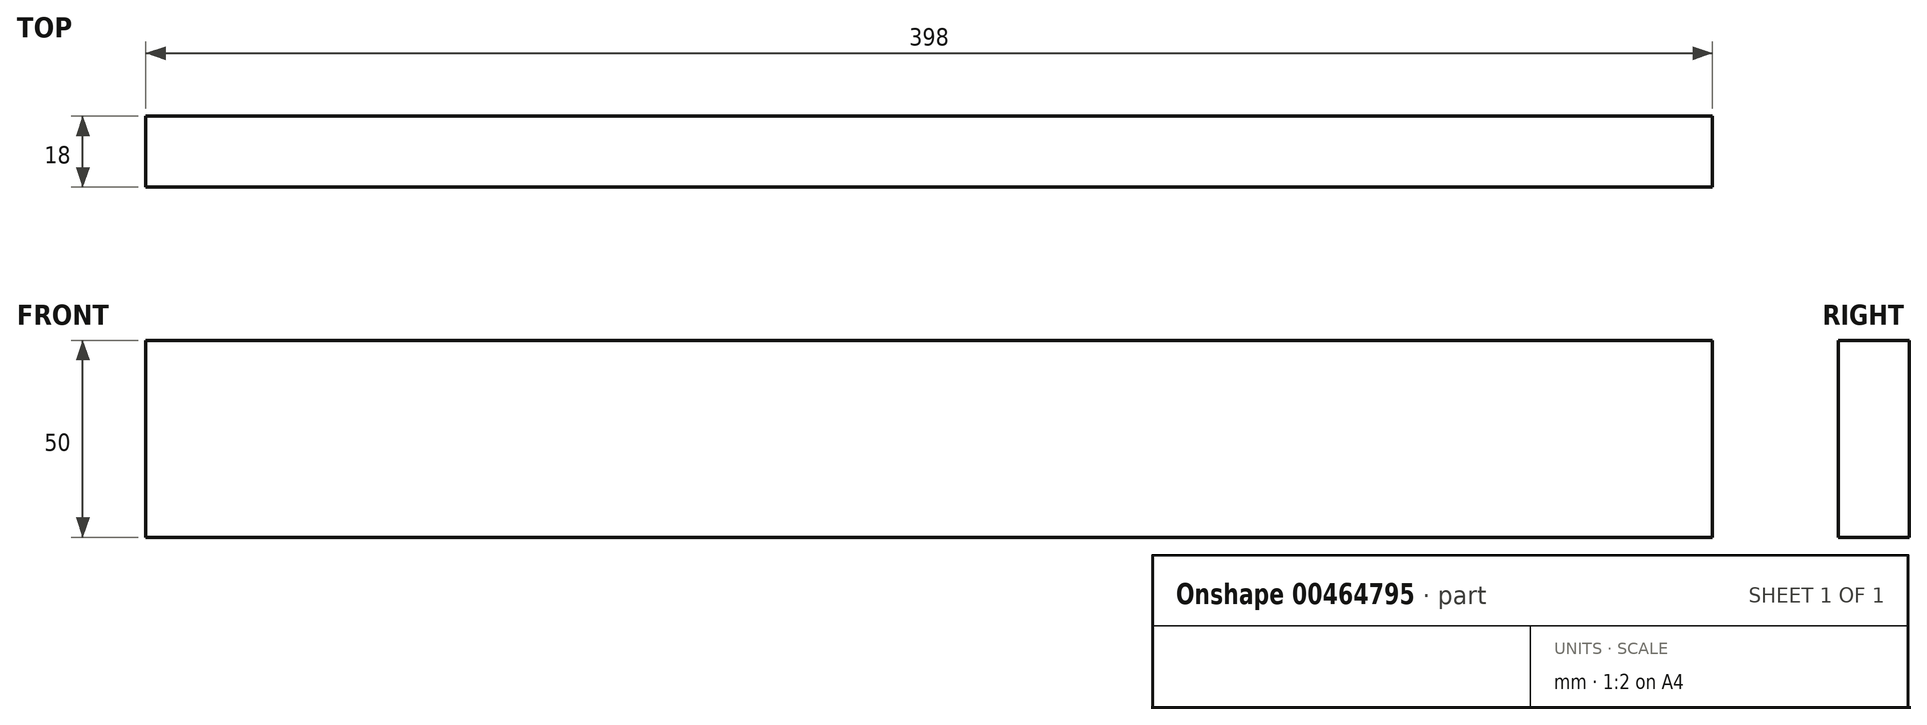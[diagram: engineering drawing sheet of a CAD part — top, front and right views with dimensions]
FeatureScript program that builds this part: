
annotation { "Feature Type Name" : "Feature", "Feature Type Description" : "" }
export const myFeature = defineFeature(function(context is Context, id is Id, definition is map)
    precondition{}
    {
        {
            var Q0;
            Q0=qCreatedBy(makeId("Front.planeOp"),FACE);
            var sketch = newSketch(context, id + "F0", { "sketchPlane" : qUnion([Q0])});
            skLineSegment(sketch, "E0.bottom", {"start": v(0, 0) * mm, "end": v(398, 0) * mm});
            skLineSegment(sketch, "E0.top", {"start": v(0, 50) * mm, "end": v(398, 50) * mm});
            skLineSegment(sketch, "E0.left", {"start": v(0, 0) * mm, "end": v(0, 50) * mm});
            skLineSegment(sketch, "E0.right", {"start": v(398, 0) * mm, "end": v(398, 50) * mm});
            skSolve(sketch);
        }
        {
            var Q0;
            Q0=qSketchRegion(id+"F0",true);
            extrude(context, id + "F1", {"entities" : qUnion([Q0]), "depth" : 18 * mm});
        }
    });
